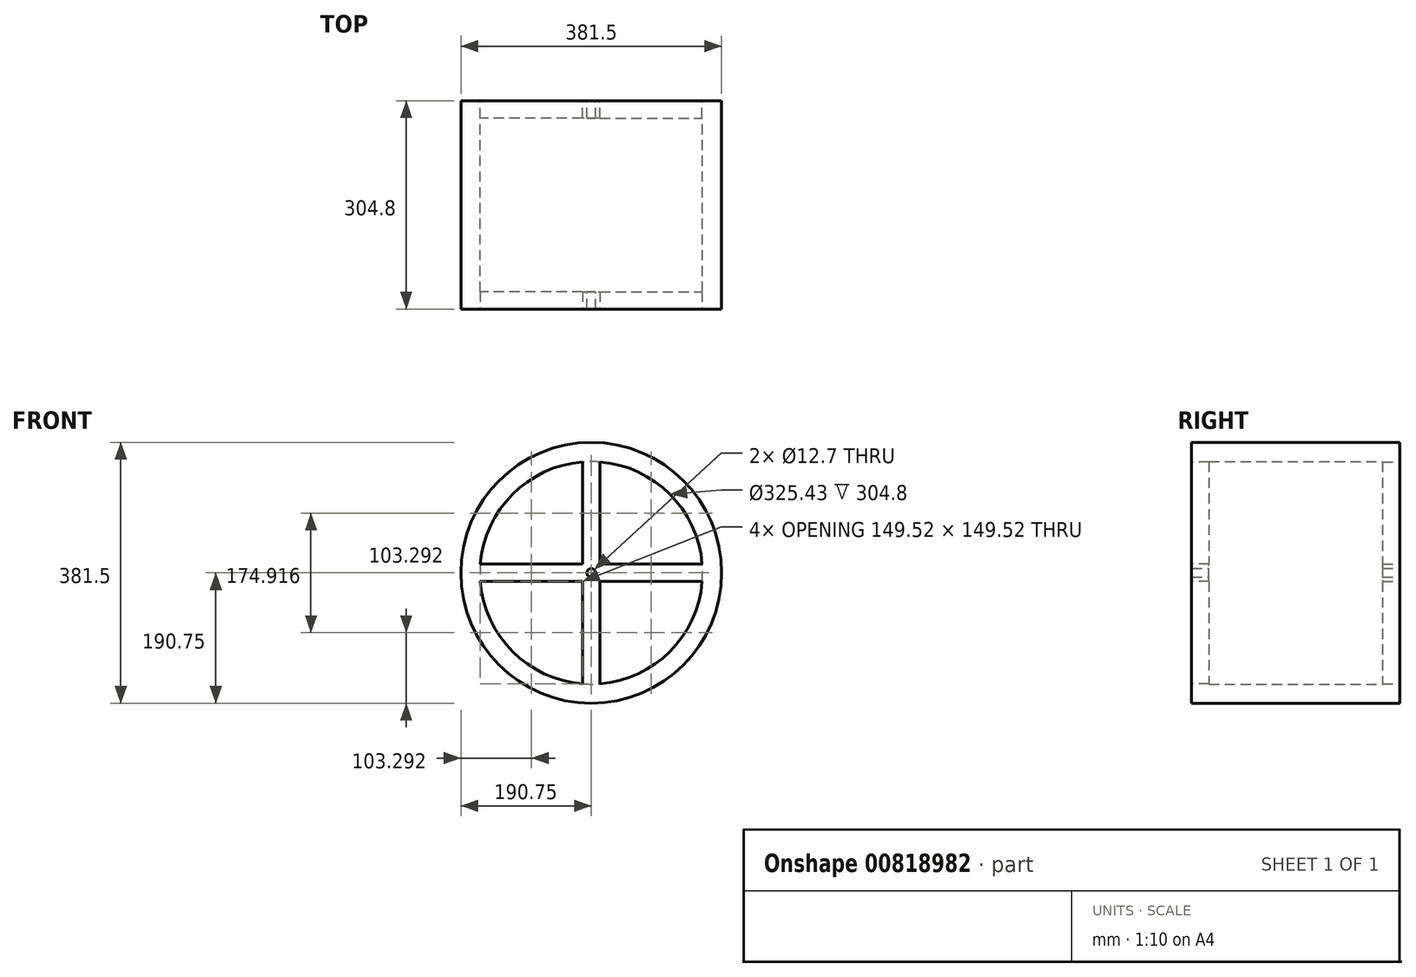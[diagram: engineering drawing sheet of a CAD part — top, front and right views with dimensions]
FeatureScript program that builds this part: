
annotation { "Feature Type Name" : "Feature", "Feature Type Description" : "" }
export const myFeature = defineFeature(function(context is Context, id is Id, definition is map)
    precondition{}
    {
        {
            var Q0;
            Q0=qCreatedBy(makeId("Front.planeOp"),FACE);
            var sketch = newSketch(context, id + "F0", { "sketchPlane" : qUnion([Q0])});
            skCircle(sketch, "E0", {"center": v(0, 0) * mm, "radius": 190.75 * mm});
            skCircle(sketch, "E1", {"center": v(0, 0) * mm, "radius": 162.71 * mm});
            skSolve(sketch);
        }
        {
            var Q0;
            Q0=makeQuery(id+"F0.imprint","IMPRINT",FACE,{"disambiguationData":[TD([[makeQuery(id+"F0.imprint","IMPRINT",EDGE,{"derivedFrom":sQuery(id+"F0.wireOp",EDGE,"E0")}),1.0]])]});
            extrude(context, id + "F1", {"entities" : qUnion([Q0]), "depth" : 304.8 * mm, "offsetDistance" : 25 * mm});
        }
        {
            var Q0;
            Q0=makeQuery(id+"F1.opExtrude","CAP_FACE",FACE,{"disambiguationData":[OSD([sQuery(id+"F0.wireOp",EDGE,"E0"),sQuery(id+"F0.wireOp",EDGE,"E1")])],"isStart":false});
            var sketch = newSketch(context, id + "F2", { "sketchPlane" : qUnion([Q0])});
            skLineSegment(sketch, "E2", {"start": v(0, 162.71) * mm, "end": v(0, -162.71) * mm, "construction": true});
            skLineSegment(sketch, "E3", {"start": v(-12.7, 162.22) * mm, "end": v(-12.7, -162.22) * mm});
            skLineSegment(sketch, "E4.MirrorCS", {"start": v(12.7, 162.22) * mm, "end": v(12.7, -162.22) * mm});
            skLineSegment(sketch, "E5", {"start": v(0, 0) * mm, "end": v(162.71, 0) * mm, "construction": true});
            skPoint(sketch, "E5.endSnap0", {"position": v(12.7, 0) * mm});
            skLineSegment(sketch, "E6", {"start": v(0, 0) * mm, "end": v(-162.71, 0) * mm, "construction": true});
            skLineSegment(sketch, "E7", {"start": v(12.7, -12.7) * mm, "end": v(162.22, -12.7) * mm});
            skLineSegment(sketch, "E8.MirrorCS", {"start": v(12.7, 12.7) * mm, "end": v(162.22, 12.7) * mm});
            skLineSegment(sketch, "E9.MirrorCS", {"start": v(-12.7, 12.7) * mm, "end": v(-162.22, 12.7) * mm});
            skLineSegment(sketch, "E10.MirrorCS", {"start": v(-12.7, -12.7) * mm, "end": v(-162.22, -12.7) * mm});
            skArc(sketch, "E11.0", {"start": v(-162.22, 12.7) * mm, "mid": v(-162.71, 0) * mm, "end": v(-162.22, -12.7) * mm});
            skArc(sketch, "E12.trimOffspring", {"start": v(12.7, 162.22) * mm, "mid": v(0, 162.71) * mm, "end": v(-12.7, 162.22) * mm});
            skArc(sketch, "E13.trimOffspring", {"start": v(162.22, -12.7) * mm, "mid": v(162.71, 0) * mm, "end": v(162.22, 12.7) * mm});
            skArc(sketch, "E14.trimOffspring", {"start": v(-12.7, -162.22) * mm, "mid": v(0, -162.71) * mm, "end": v(12.7, -162.22) * mm});
            skSolve(sketch);
        }
        {
            var Q0;
            Q0=qSketchRegion(id+"F2",true);
            var Q1;
            {var subQ0=sQuery(id+"F2.wireOp",EDGE,"E9.MirrorCS");Q1=makeQuery(id+"F2.imprint","IMPRINT",FACE,{"disambiguationData":[TD([[makeQuery(id+"F2.imprint","IMPRINT",EDGE,{"derivedFrom":subQ0}),1.0]])]});}
            var Q2;
            {var subQ0=sQuery(id+"F2.wireOp",EDGE,"E7");Q2=makeQuery(id+"F2.imprint","IMPRINT",FACE,{"disambiguationData":[TD([[makeQuery(id+"F2.imprint","IMPRINT",EDGE,{"derivedFrom":subQ0}),1.0]])]});}
            var Q3;
            {var subQ1=makeQuery(id+"F1.opExtrude","CAP_EDGE",EDGE,{"disambiguationData":[OSD([sQuery(id+"F0.wireOp",EDGE,"E1")])],"isStart":false});var subQ4=sQuery(id+"F2.wireOp",EDGE,"E3");var subQ9=makeQuery(id+"F2.imprint","INTERSECT",VERTEX,{"disambiguationData":[OD(0.0)],"derivedFrom":[subQ1,subQ4]});Q3=makeQuery(id+"F2.imprint","IMPRINT",FACE,{"disambiguationData":[TD([[makeQuery(id+"F2.imprint","IMPRINT",EDGE,{"disambiguationData":[TD([[subQ9,-1.0]])],"derivedFrom":subQ4}),1.0]])]});}
            extrude(context, id + "F3", {"entities" : qUnion([Q0, Q1, Q2, Q3]), "operationType" : NewBodyOperationType.ADD, "oppositeDirection" : true, "depth" : 25.4 * mm, "offsetDistance" : 25 * mm});
        }
        {
            var Q0;
            Q0=makeQuery(id+"F1.opExtrude","CAP_FACE",FACE,{"disambiguationData":[OSD([sQuery(id+"F0.wireOp",EDGE,"E0"),sQuery(id+"F0.wireOp",EDGE,"E1")])],"isStart":true});
            var sketch = newSketch(context, id + "F4", { "sketchPlane" : qUnion([Q0])});
            skLineSegment(sketch, "E15.0", {"start": v(-12.7, 12.7) * mm, "end": v(-162.22, 12.7) * mm});
            skLineSegment(sketch, "E15.1", {"start": v(-12.7, 162.22) * mm, "end": v(-12.7, 12.7) * mm});
            skLineSegment(sketch, "E15.2", {"start": v(12.7, 162.22) * mm, "end": v(12.7, 12.7) * mm});
            skLineSegment(sketch, "E15.3", {"start": v(12.7, 12.7) * mm, "end": v(162.22, 12.7) * mm});
            skLineSegment(sketch, "E15.4", {"start": v(12.7, -12.7) * mm, "end": v(162.22, -12.7) * mm});
            skLineSegment(sketch, "E15.5", {"start": v(12.7, -12.7) * mm, "end": v(12.7, -162.22) * mm});
            skLineSegment(sketch, "E15.6", {"start": v(-12.7, -12.7) * mm, "end": v(-12.7, -162.22) * mm});
            skLineSegment(sketch, "E15.7", {"start": v(-12.7, -12.7) * mm, "end": v(-162.22, -12.7) * mm});
            skArc(sketch, "E16.0", {"start": v(-162.22, 12.7) * mm, "mid": v(-162.71, 0) * mm, "end": v(-162.22, -12.7) * mm});
            skArc(sketch, "E17.trimOffspring", {"start": v(12.7, 162.22) * mm, "mid": v(0, 162.71) * mm, "end": v(-12.7, 162.22) * mm});
            skArc(sketch, "E18.trimOffspring", {"start": v(162.22, -12.7) * mm, "mid": v(162.71, 0) * mm, "end": v(162.22, 12.7) * mm});
            skArc(sketch, "E19.trimOffspring", {"start": v(-12.7, -162.22) * mm, "mid": v(0, -162.71) * mm, "end": v(12.7, -162.22) * mm});
            skSolve(sketch);
        }
        {
            var Q0;
            Q0=makeQuery(id+"F4.imprint","IMPRINT",FACE,{"disambiguationData":[TD([[makeQuery(id+"F4.imprint","IMPRINT",EDGE,{"derivedFrom":sQuery(id+"F4.wireOp",EDGE,"E15.0")}),1.0]])]});
            extrude(context, id + "F5", {"entities" : qUnion([Q0]), "operationType" : NewBodyOperationType.ADD, "oppositeDirection" : true, "depth" : 25.4 * mm, "offsetDistance" : 25 * mm});
        }
        {
            var Q0;
            Q0=makeQuery(id+"F5.boolean.opBoolean","MERGE",FACE,{"derivedFrom":[makeQuery(id+"F1.opExtrude","CAP_FACE",FACE,{"disambiguationData":[OSD([sQuery(id+"F0.wireOp",EDGE,"E0"),sQuery(id+"F0.wireOp",EDGE,"E1")])],"isStart":true}),makeQuery(id+"F5.opExtrude","CAP_FACE",FACE,{"disambiguationData":[OSD([sQuery(id+"F4.wireOp",EDGE,"E15.0"),sQuery(id+"F4.wireOp",EDGE,"E15.1"),sQuery(id+"F4.wireOp",EDGE,"E15.2"),sQuery(id+"F4.wireOp",EDGE,"E15.3"),sQuery(id+"F4.wireOp",EDGE,"E15.4"),sQuery(id+"F4.wireOp",EDGE,"E15.5"),sQuery(id+"F4.wireOp",EDGE,"E15.6"),sQuery(id+"F4.wireOp",EDGE,"E15.7"),sQuery(id+"F4.wireOp",EDGE,"E16.0"),sQuery(id+"F4.wireOp",EDGE,"E17.trimOffspring"),sQuery(id+"F4.wireOp",EDGE,"E18.trimOffspring"),sQuery(id+"F4.wireOp",EDGE,"E19.trimOffspring")])],"isStart":true})]});
            var sketch = newSketch(context, id + "F6", { "sketchPlane" : qUnion([Q0])});
            skCircle(sketch, "E20", {"center": v(0, 0) * mm, "radius": 6.35 * mm});
            skSolve(sketch);
        }
        {
            var Q0;
            Q0=makeQuery(id+"F6.imprint","IMPRINT",FACE,{"disambiguationData":[TD([[makeQuery(id+"F6.imprint","IMPRINT",EDGE,{"derivedFrom":sQuery(id+"F6.wireOp",EDGE,"E20")}),1.0]])]});
            extrude(context, id + "F7", {"entities" : qUnion([Q0]), "operationType" : NewBodyOperationType.REMOVE, "oppositeDirection" : true, "depth" : 382 * mm, "offsetDistance" : 25 * mm});
        }
    });
